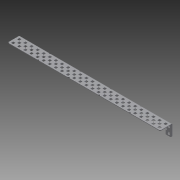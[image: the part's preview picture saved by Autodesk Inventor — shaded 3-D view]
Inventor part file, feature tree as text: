
AUTODESK INVENTOR PART (.ipt)
format: ipt  version: 2014 SP1 (Build 180222100, 222)  size: 1,654,784 bytes
history: native  units: in
note: dims shown in document units (in); Inventor stores cm internally (conversion verified against a paired STEP export)
features: other x1, imported_body x1, extrude x1, sketch x1
ambient origin geometry x8: Origin, YZ Plane, XZ Plane, XY Plane, X Axis, Y Axis, Z Axis, Center Point
bodies: Body1 (feature_tree)
feature tree (4):
  parser-record x1  (decoder bookkeeping rows leaked as tree rows — omitted from the tree; the rows remain in map.json)
  imported_body  "Base1"
  extrude  "Extrusion1"  Depth=2.0in
  sketch  "Sketch1"  dims[d0=0.5in d1=2.0in d2=0.5in d3=6.25in d4=1.0in d5=0.0in]
